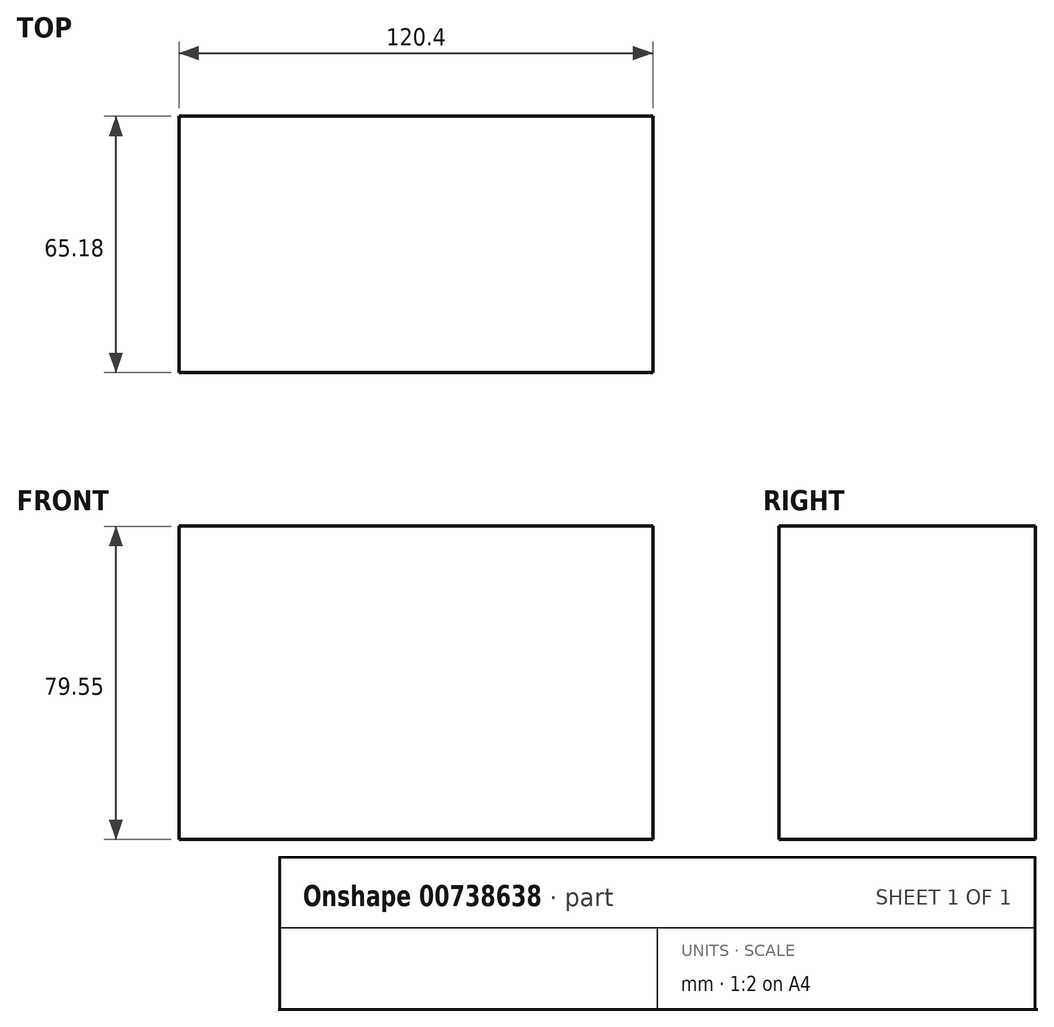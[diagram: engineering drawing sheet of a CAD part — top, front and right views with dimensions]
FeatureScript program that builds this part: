
annotation { "Feature Type Name" : "Feature", "Feature Type Description" : "" }
export const myFeature = defineFeature(function(context is Context, id is Id, definition is map)
    precondition{}
    {
        {
            var Q0;
            Q0=qCreatedBy(makeId("Front.planeOp"),FACE);
            var sketch = newSketch(context, id + "F0", { "sketchPlane" : qUnion([Q0])});
            skLineSegment(sketch, "E0.bottom", {"start": v(-59.8, 22.2) * mm, "end": v(60.59, 22.2) * mm});
            skLineSegment(sketch, "E0.top", {"start": v(-59.8, -57.35) * mm, "end": v(60.59, -57.35) * mm});
            skLineSegment(sketch, "E0.left", {"start": v(-59.8, 22.2) * mm, "end": v(-59.8, -57.35) * mm});
            skLineSegment(sketch, "E0.right", {"start": v(60.59, 22.2) * mm, "end": v(60.59, -57.35) * mm});
            skSolve(sketch);
        }
        {
            var Q0;
            Q0=qCreatedBy(makeId("Front.planeOp"),FACE);
            var sketch = newSketch(context, id + "F1", { "sketchPlane" : qUnion([Q0])});
            skLineSegment(sketch, "E1", {"start": v(-63.6, 21.9) * mm, "end": v(0, 74.3) * mm});
            skLineSegment(sketch, "E2", {"start": v(0, 74.3) * mm, "end": v(60.75, 21.7) * mm});
            skSolve(sketch);
        }
        {
            var Q0;
            Q0 = qSketchRegion(id + "F0", true);
            var Q1;
            Q1 = qSketchRegion(id + "F1", true);
            extrude(context, id + "F2", {"entities" : qUnion([Q0, Q1]), "oppositeDirection" : true, "depth" : 65.18 * mm, "offsetDistance" : 25.4 * mm});
        }
        {
            var Q0;
            Q0=sQuery(id+"F1.wireOp",EDGE,"E2");
            var Q1;
            Q1=sQuery(id+"F1.wireOp",EDGE,"E1");
            extrude(context, id + "F3", {"bodyType" : ToolBodyType.SURFACE, "surfaceEntities" : qUnion([Q0, Q1]), "oppositeDirection" : true, "depth" : 83.02 * mm, "offsetDistance" : 25.4 * mm});
        }
    });
